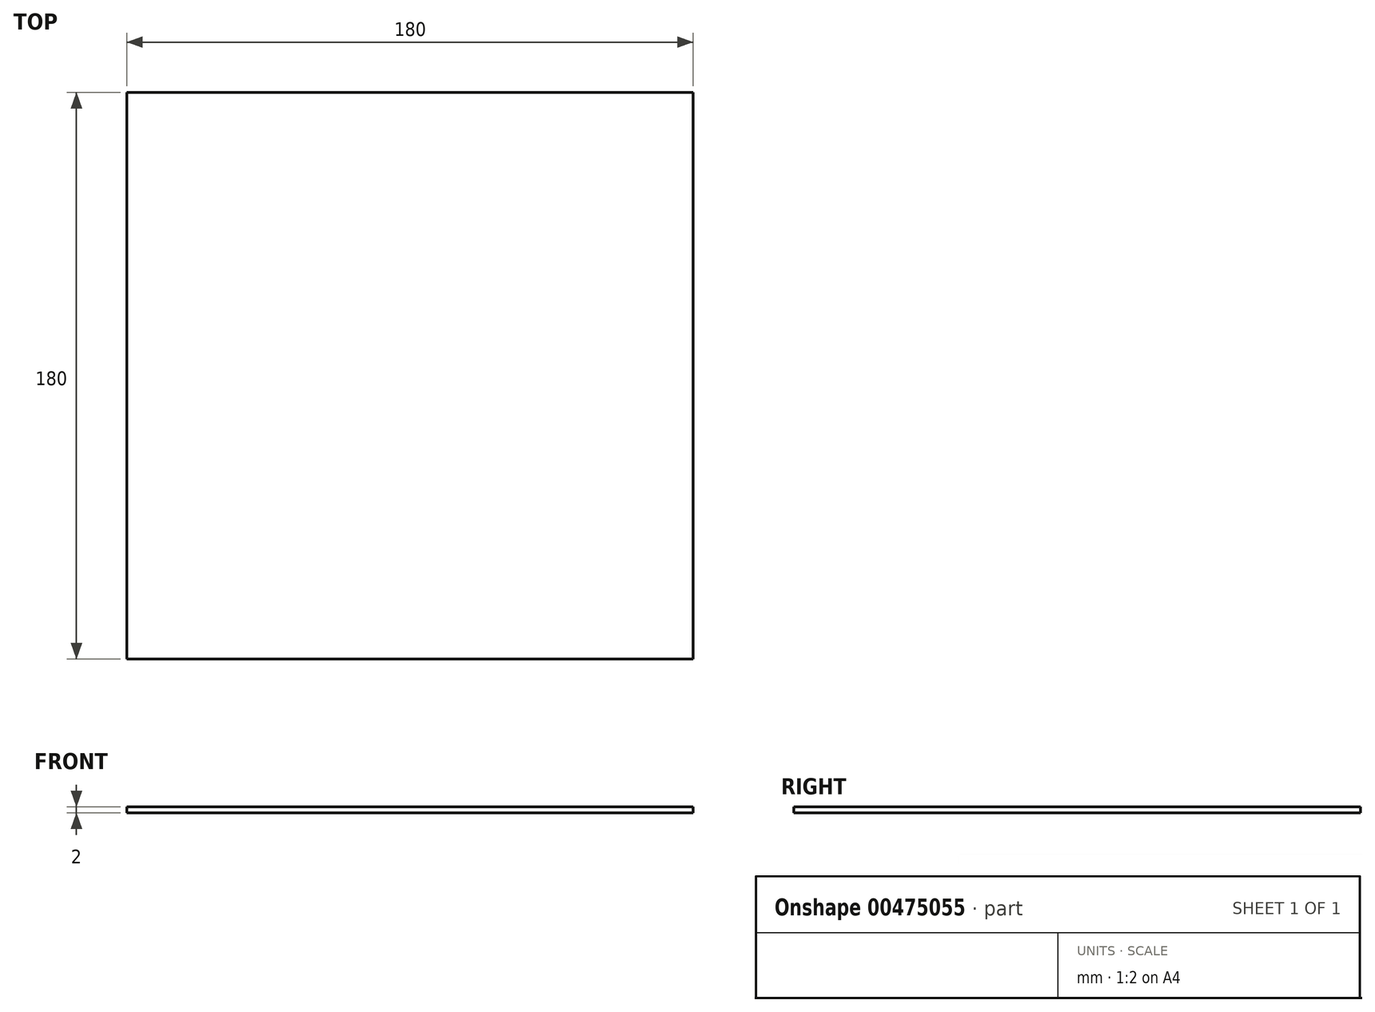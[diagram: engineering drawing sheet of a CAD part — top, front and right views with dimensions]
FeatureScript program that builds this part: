
annotation { "Feature Type Name" : "Feature", "Feature Type Description" : "" }
export const myFeature = defineFeature(function(context is Context, id is Id, definition is map)
    precondition{}
    {
        {
            var Q0;
            Q0=qCreatedBy(makeId("Top.planeOp"),FACE);
            var sketch = newSketch(context, id + "F0", { "sketchPlane" : qUnion([Q0])});
            skLineSegment(sketch, "E0.bottom", {"start": v(-99.8, 112.6) * mm, "end": v(80.2, 112.6) * mm});
            skLineSegment(sketch, "E0.top", {"start": v(-99.8, -67.4) * mm, "end": v(80.2, -67.4) * mm});
            skLineSegment(sketch, "E0.left", {"start": v(-99.8, 112.6) * mm, "end": v(-99.8, -67.4) * mm});
            skLineSegment(sketch, "E0.right", {"start": v(80.2, 112.6) * mm, "end": v(80.2, -67.4) * mm});
            skSolve(sketch);
        }
        {
            var Q0;
            Q0 = qSketchRegion(id + "F0", true);
            extrude(context, id + "F1", {"entities" : qUnion([Q0]), "depth" : 2 * mm});
        }
    });
